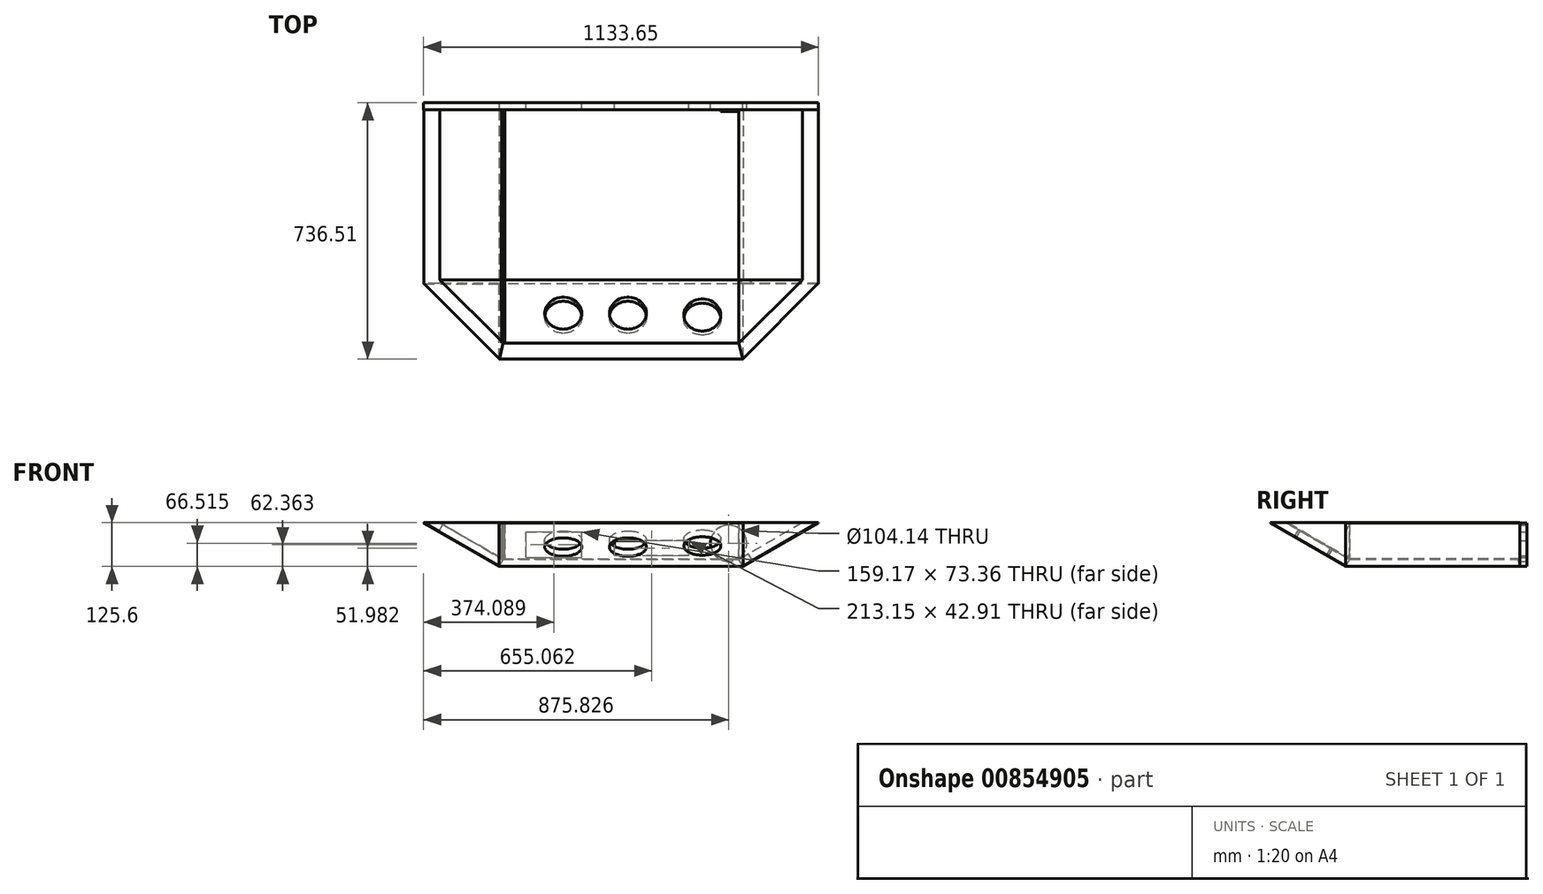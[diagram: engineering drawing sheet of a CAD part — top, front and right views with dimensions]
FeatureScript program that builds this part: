
annotation { "Feature Type Name" : "Feature", "Feature Type Description" : "" }
export const myFeature = defineFeature(function(context is Context, id is Id, definition is map)
    precondition{}
    {
        {
            var Q0;
            Q0=qCreatedBy(makeId("Top.planeOp"),FACE);
            var sketch = newSketch(context, id + "F0", { "sketchPlane" : qUnion([Q0])});
            skLineSegment(sketch, "E0.bottom", {"start": v(350, 250) * mm, "end": v(-350, 250) * mm});
            skLineSegment(sketch, "E0.top", {"start": v(350, -250) * mm, "end": v(-350, -250) * mm});
            skLineSegment(sketch, "E0.left", {"start": v(350, 250) * mm, "end": v(350, -250) * mm});
            skLineSegment(sketch, "E0.right", {"start": v(-350, 250) * mm, "end": v(-350, -250) * mm});
            skPoint(sketch, "E0.middle", {"position": v(0, 0) * mm});
            skSolve(sketch);
        }
        {
            var Q0;
            Q0=makeQuery(id+"F0.imprint","IMPRINT",FACE,{"disambiguationData":[TD([[makeQuery(id+"F0.imprint","IMPRINT",EDGE,{"derivedFrom":sQuery(id+"F0.wireOp",EDGE,"E0.bottom")}),1.0]])]});
            extrude(context, id + "F1", {"entities" : qUnion([Q0]), "depth" : 20 * mm, "offsetDistance" : 25 * mm});
        }
        {
            var Q0;
            Q0=makeQuery(id+"F1.opExtrude","CAP_EDGE",EDGE,{"disambiguationData":[OSD([sQuery(id+"F0.wireOp",EDGE,"E0.right")])],"isStart":false});
            var Q1;
            Q1=makeQuery(id+"F1.opExtrude","CAP_EDGE",EDGE,{"disambiguationData":[OSD([sQuery(id+"F0.wireOp",EDGE,"E0.top")])],"isStart":false});
            var Q2;
            Q2=makeQuery(id+"F1.opExtrude","CAP_EDGE",EDGE,{"disambiguationData":[OSD([sQuery(id+"F0.wireOp",EDGE,"E0.left")])],"isStart":false});
            chamfer(context, id + "F2", {"entities" : qUnion([Q0, Q1, Q2]), "chamferType" : ChamferType.OFFSET_ANGLE, "width" : 20 * mm, "oppositeDirection" : true, "angle" : 30 * degree, "tangentPropagation" : true});
        }
        {
            var Q0;
            Q0=makeQuery(id+"F2.opChamfer","BLEND_FACE",FACE,{"disambiguationData":[OSD([sQuery(id+"F0.wireOp",EDGE,"E0.top")])]});
            extrude(context, id + "F3", {"entities" : qUnion([Q0]), "operationType" : NewBodyOperationType.ADD, "depth" : 250 * mm, "offsetDistance" : 25 * mm});
        }
        {
            var Q0;
            Q0=makeQuery(id+"F2.opChamfer","BLEND_FACE",FACE,{"disambiguationData":[OSD([sQuery(id+"F0.wireOp",EDGE,"E0.right")])]});
            extrude(context, id + "F4", {"entities" : qUnion([Q0]), "operationType" : NewBodyOperationType.ADD, "depth" : 250 * mm, "offsetDistance" : 25 * mm});
        }
        {
            var Q0;
            Q0=makeQuery(id+"F2.opChamfer","BLEND_FACE",FACE,{"disambiguationData":[OSD([sQuery(id+"F0.wireOp",EDGE,"E0.left")])]});
            extrude(context, id + "F5", {"entities" : qUnion([Q0]), "operationType" : NewBodyOperationType.ADD, "depth" : 250 * mm, "offsetDistance" : 25 * mm});
        }
        {
            var Q0;
            {var subQ0=sQuery(id+"F0.wireOp",EDGE,"E0.right");var subQ1=sQuery(id+"F0.wireOp",EDGE,"E0.left");var subQ2=sQuery(id+"F0.wireOp",EDGE,"E0.top");var subQ3=sQuery(id+"F0.wireOp",EDGE,"E0.bottom");var subQ4=makeQuery(id+"F2.opChamfer","BLEND_VERTEX",VERTEX,{"blendedFrom":[makeQuery(id+"F1.opExtrude","CAP_EDGE",EDGE,{"disambiguationData":[OSD([subQ2])],"isStart":false}),makeQuery(id+"F1.opExtrude","CAP_EDGE",EDGE,{"disambiguationData":[OSD([subQ1])],"isStart":false}),makeQuery(id+"F1.opExtrude","CAP_FACE",FACE,{"disambiguationData":[OSD([subQ3,subQ2,subQ1,subQ0])],"isStart":false})],"blendedInto":[makeQuery(id+"F1.opExtrude","CAP_FACE",FACE,{"disambiguationData":[OSD([subQ3,subQ2,subQ1,subQ0])],"isStart":false})]});var subQ5=makeQuery(id+"F3.boolean.opBoolean","MERGE",VERTEX,{"derivedFrom":[subQ4,makeQuery(id+"F3.opExtrude","CAP_VERTEX",VERTEX,{"disambiguationData":[OSD([subQ3,subQ2,subQ1,subQ0]),TDD([subQ4])],"isStart":true})]});Q0=makeQuery(id+"F5.boolean.opBoolean","MERGE",VERTEX,{"derivedFrom":[subQ5,makeQuery(id+"F5.opExtrude","CAP_VERTEX",VERTEX,{"disambiguationData":[OSD([subQ3,subQ2,subQ1,subQ0]),TDD([subQ5])],"isStart":true})]});}
            var Q1;
            {var subQ0=sQuery(id+"F0.wireOp",EDGE,"E0.right");var subQ1=sQuery(id+"F0.wireOp",EDGE,"E0.left");var subQ2=sQuery(id+"F0.wireOp",EDGE,"E0.top");var subQ3=sQuery(id+"F0.wireOp",EDGE,"E0.bottom");Q1=makeQuery(id+"F3.opExtrude","CAP_VERTEX",VERTEX,{"disambiguationData":[OSD([subQ3,subQ2,subQ1,subQ0]),TDD([makeQuery(id+"F2.opChamfer","BLEND_VERTEX",VERTEX,{"blendedFrom":[makeQuery(id+"F1.opExtrude","CAP_EDGE",EDGE,{"disambiguationData":[OSD([subQ2])],"isStart":false}),makeQuery(id+"F1.opExtrude","CAP_EDGE",EDGE,{"disambiguationData":[OSD([subQ1])],"isStart":false}),makeQuery(id+"F1.opExtrude","CAP_FACE",FACE,{"disambiguationData":[OSD([subQ3,subQ2,subQ1,subQ0])],"isStart":false})],"blendedInto":[makeQuery(id+"F1.opExtrude","CAP_FACE",FACE,{"disambiguationData":[OSD([subQ3,subQ2,subQ1,subQ0])],"isStart":false})]})])],"isStart":false});}
            var Q2;
            {var subQ0=sQuery(id+"F0.wireOp",EDGE,"E0.right");var subQ1=sQuery(id+"F0.wireOp",EDGE,"E0.left");var subQ2=sQuery(id+"F0.wireOp",EDGE,"E0.top");var subQ3=sQuery(id+"F0.wireOp",EDGE,"E0.bottom");var subQ4=makeQuery(id+"F2.opChamfer","BLEND_VERTEX",VERTEX,{"blendedFrom":[makeQuery(id+"F1.opExtrude","CAP_EDGE",EDGE,{"disambiguationData":[OSD([subQ2])],"isStart":false}),makeQuery(id+"F1.opExtrude","CAP_EDGE",EDGE,{"disambiguationData":[OSD([subQ1])],"isStart":false}),makeQuery(id+"F1.opExtrude","CAP_FACE",FACE,{"disambiguationData":[OSD([subQ3,subQ2,subQ1,subQ0])],"isStart":false})],"blendedInto":[makeQuery(id+"F1.opExtrude","CAP_FACE",FACE,{"disambiguationData":[OSD([subQ3,subQ2,subQ1,subQ0])],"isStart":false})]});Q2=makeQuery(id+"F5.opExtrude","CAP_VERTEX",VERTEX,{"disambiguationData":[OSD([subQ3,subQ2,subQ1,subQ0]),TDD([makeQuery(id+"F3.boolean.opBoolean","MERGE",VERTEX,{"derivedFrom":[subQ4,makeQuery(id+"F3.opExtrude","CAP_VERTEX",VERTEX,{"disambiguationData":[OSD([subQ3,subQ2,subQ1,subQ0]),TDD([subQ4])],"isStart":true})]})])],"isStart":false});}
            cPlane(context, id + "F6", {"entities" : qUnion([Q0, Q1, Q2]), "cplaneType" : CPlaneType.THREE_POINT, "offset" : 0 * mm, "width" : 150 * mm, "height" : 150 * mm});
        }
        {
            var Q0;
            Q0=qCreatedBy(id+"F6.planeOp",FACE);
            var sketch = newSketch(context, id + "F7", { "sketchPlane" : qUnion([Q0])});
            skLineSegment(sketch, "E1", {"start": v(499.22, 278.94) * mm, "end": v(257.18, 216.53) * mm});
            skLineSegment(sketch, "E2", {"start": v(257.18, 216.53) * mm, "end": v(257.18, 466.29) * mm});
            skLineSegment(sketch, "E3", {"start": v(257.18, 466.29) * mm, "end": v(499.22, 278.94) * mm});
            skSolve(sketch);
        }
        {
            var Q0;
            Q0=makeQuery(id+"F7.imprint","IMPRINT",FACE,{"disambiguationData":[TD([[makeQuery(id+"F7.imprint","IMPRINT",EDGE,{"derivedFrom":sQuery(id+"F7.wireOp",EDGE,"E1")}),-1.0]])]});
            extrude(context, id + "F8", {"entities" : qUnion([Q0]), "operationType" : NewBodyOperationType.ADD, "depth" : 25 * mm, "offsetDistance" : 25 * mm});
        }
        {
            var Q0;
            {var subQ0=sQuery(id+"F0.wireOp",EDGE,"E0.right");var subQ1=sQuery(id+"F0.wireOp",EDGE,"E0.left");var subQ2=sQuery(id+"F0.wireOp",EDGE,"E0.top");var subQ3=sQuery(id+"F0.wireOp",EDGE,"E0.bottom");var subQ4=makeQuery(id+"F2.opChamfer","BLEND_VERTEX",VERTEX,{"blendedFrom":[makeQuery(id+"F1.opExtrude","CAP_EDGE",EDGE,{"disambiguationData":[OSD([subQ2])],"isStart":false}),makeQuery(id+"F1.opExtrude","CAP_EDGE",EDGE,{"disambiguationData":[OSD([subQ0])],"isStart":false}),makeQuery(id+"F1.opExtrude","CAP_FACE",FACE,{"disambiguationData":[OSD([subQ3,subQ2,subQ1,subQ0])],"isStart":false})],"blendedInto":[makeQuery(id+"F1.opExtrude","CAP_FACE",FACE,{"disambiguationData":[OSD([subQ3,subQ2,subQ1,subQ0])],"isStart":false})]});Q0=makeQuery(id+"F4.opExtrude","CAP_VERTEX",VERTEX,{"disambiguationData":[OSD([subQ3,subQ2,subQ1,subQ0]),TDD([makeQuery(id+"F3.boolean.opBoolean","MERGE",VERTEX,{"derivedFrom":[subQ4,makeQuery(id+"F3.opExtrude","CAP_VERTEX",VERTEX,{"disambiguationData":[OSD([subQ3,subQ2,subQ1,subQ0]),TDD([subQ4])],"isStart":true})]})])],"isStart":false});}
            var Q1;
            {var subQ0=sQuery(id+"F0.wireOp",EDGE,"E0.right");var subQ1=sQuery(id+"F0.wireOp",EDGE,"E0.left");var subQ2=sQuery(id+"F0.wireOp",EDGE,"E0.top");var subQ3=sQuery(id+"F0.wireOp",EDGE,"E0.bottom");var subQ4=makeQuery(id+"F2.opChamfer","BLEND_VERTEX",VERTEX,{"blendedFrom":[makeQuery(id+"F1.opExtrude","CAP_EDGE",EDGE,{"disambiguationData":[OSD([subQ2])],"isStart":false}),makeQuery(id+"F1.opExtrude","CAP_EDGE",EDGE,{"disambiguationData":[OSD([subQ0])],"isStart":false}),makeQuery(id+"F1.opExtrude","CAP_FACE",FACE,{"disambiguationData":[OSD([subQ3,subQ2,subQ1,subQ0])],"isStart":false})],"blendedInto":[makeQuery(id+"F1.opExtrude","CAP_FACE",FACE,{"disambiguationData":[OSD([subQ3,subQ2,subQ1,subQ0])],"isStart":false})]});var subQ5=makeQuery(id+"F3.boolean.opBoolean","MERGE",VERTEX,{"derivedFrom":[subQ4,makeQuery(id+"F3.opExtrude","CAP_VERTEX",VERTEX,{"disambiguationData":[OSD([subQ3,subQ2,subQ1,subQ0]),TDD([subQ4])],"isStart":true})]});Q1=makeQuery(id+"F4.boolean.opBoolean","MERGE",VERTEX,{"derivedFrom":[subQ5,makeQuery(id+"F4.opExtrude","CAP_VERTEX",VERTEX,{"disambiguationData":[OSD([subQ3,subQ2,subQ1,subQ0]),TDD([subQ5])],"isStart":true})]});}
            var Q2;
            {var subQ0=sQuery(id+"F0.wireOp",EDGE,"E0.right");var subQ1=sQuery(id+"F0.wireOp",EDGE,"E0.left");var subQ2=sQuery(id+"F0.wireOp",EDGE,"E0.top");var subQ3=sQuery(id+"F0.wireOp",EDGE,"E0.bottom");Q2=makeQuery(id+"F3.opExtrude","CAP_VERTEX",VERTEX,{"disambiguationData":[OSD([subQ3,subQ2,subQ1,subQ0]),TDD([makeQuery(id+"F2.opChamfer","BLEND_VERTEX",VERTEX,{"blendedFrom":[makeQuery(id+"F1.opExtrude","CAP_EDGE",EDGE,{"disambiguationData":[OSD([subQ2])],"isStart":false}),makeQuery(id+"F1.opExtrude","CAP_EDGE",EDGE,{"disambiguationData":[OSD([subQ0])],"isStart":false}),makeQuery(id+"F1.opExtrude","CAP_FACE",FACE,{"disambiguationData":[OSD([subQ3,subQ2,subQ1,subQ0])],"isStart":false})],"blendedInto":[makeQuery(id+"F1.opExtrude","CAP_FACE",FACE,{"disambiguationData":[OSD([subQ3,subQ2,subQ1,subQ0])],"isStart":false})]})])],"isStart":false});}
            cPlane(context, id + "F9", {"entities" : qUnion([Q0, Q1, Q2]), "cplaneType" : CPlaneType.THREE_POINT, "offset" : 25 * mm, "width" : 150 * mm, "height" : 150 * mm});
        }
        {
            var Q0;
            Q0=qCreatedBy(id+"F9.planeOp",FACE);
            var sketch = newSketch(context, id + "F10", { "sketchPlane" : qUnion([Q0])});
            skLineSegment(sketch, "E4", {"start": v(-257.22, -466.76) * mm, "end": v(-257.22, -216.6) * mm});
            skLineSegment(sketch, "E5", {"start": v(-257.22, -216.6) * mm, "end": v(-499.42, -279.04) * mm});
            skLineSegment(sketch, "E6", {"start": v(-499.42, -279.04) * mm, "end": v(-257.22, -466.76) * mm});
            skSolve(sketch);
        }
        {
            var Q0;
            Q0=makeQuery(id+"F10.imprint","IMPRINT",FACE,{"disambiguationData":[TD([[makeQuery(id+"F10.imprint","IMPRINT",EDGE,{"derivedFrom":sQuery(id+"F10.wireOp",EDGE,"E4")}),1.0]])]});
            extrude(context, id + "F11", {"entities" : qUnion([Q0]), "operationType" : NewBodyOperationType.ADD, "oppositeDirection" : true, "depth" : 25 * mm, "offsetDistance" : 25 * mm});
        }
        {
            var Q0;
            {var subQ0=sQuery(id+"F0.wireOp",EDGE,"E0.bottom");Q0=makeQuery(id+"F5.boolean.opBoolean","MERGE",FACE,{"derivedFrom":[makeQuery(id+"F4.boolean.opBoolean","MERGE",FACE,{"derivedFrom":[makeQuery(id+"F1.opExtrude","SWEPT_FACE",FACE,{"disambiguationData":[OSD([subQ0])]}),makeQuery(id+"F4.opExtrude","SWEPT_FACE",FACE,{"disambiguationData":[OSD([subQ0,sQuery(id+"F0.wireOp",EDGE,"E0.right")])]})]}),makeQuery(id+"F5.opExtrude","SWEPT_FACE",FACE,{"disambiguationData":[OSD([subQ0,sQuery(id+"F0.wireOp",EDGE,"E0.left")])]})]});}
            var Q1;
            Q1 = qBodyType(qCreatedBy(id + "F13" ,EDGE), BodyType.WIRE);
            cPlane(context, id + "F12", {"entities" : qUnion([Q0, Q1]), "cplaneType" : CPlaneType.OFFSET, "offset" : 0 * mm, "width" : 150 * mm, "height" : 150 * mm});
        }
        {
            var Q0;
            Q0=qCreatedBy(id+"F12.planeOp",FACE);
            var sketch = newSketch(context, id + "F13", { "sketchPlane" : qUnion([Q0])});
            skLineSegment(sketch, "E7", {"start": v(-566.59, 125.24) * mm, "end": v(567.06, 125.24) * mm});
            skLineSegment(sketch, "E8", {"start": v(567.06, 125.24) * mm, "end": v(349.95, 0) * mm});
            skLineSegment(sketch, "E9", {"start": v(349.95, 0) * mm, "end": v(-347.9, 0) * mm});
            skLineSegment(sketch, "E10", {"start": v(-347.9, 0) * mm, "end": v(-566.59, 125.24) * mm});
            skSolve(sketch);
        }
        {
            var Q0;
            Q0=makeQuery(id+"F13.imprint","IMPRINT",FACE,{"disambiguationData":[TD([[makeQuery(id+"F13.imprint","IMPRINT",EDGE,{"derivedFrom":sQuery(id+"F13.wireOp",EDGE,"E7")}),-1.0]])]});
            extrude(context, id + "F14", {"entities" : qUnion([Q0]), "depth" : 20 * mm, "offsetDistance" : 25 * mm});
        }
        {
            var Q0;
            Q0=qCreatedBy(id+"F12.planeOp",FACE);
            var sketch = newSketch(context, id + "F15", { "sketchPlane" : qUnion([Q0])});
            skLineSegment(sketch, "E11.bottom", {"start": v(-566.55, 125.42) * mm, "end": v(567.42, 125.42) * mm});
            skLineSegment(sketch, "E11.top", {"start": v(-566.55, 149.99) * mm, "end": v(567.42, 149.99) * mm});
            skLineSegment(sketch, "E11.left", {"start": v(-566.55, 125.42) * mm, "end": v(-566.55, 149.99) * mm});
            skLineSegment(sketch, "E11.right", {"start": v(567.42, 125.42) * mm, "end": v(567.42, 149.99) * mm});
            skSolve(sketch);
        }
        {
            var Q0;
            Q0=makeQuery(id+"F15.imprint","IMPRINT",FACE,{"disambiguationData":[TD([[makeQuery(id+"F15.imprint","IMPRINT",EDGE,{"derivedFrom":sQuery(id+"F15.wireOp",EDGE,"E11.bottom")}),1.0]])]});
            extrude(context, id + "F16", {"entities" : qUnion([Q0]), "operationType" : NewBodyOperationType.REMOVE, "oppositeDirection" : true, "depth" : 800 * mm, "offsetDistance" : 25 * mm});
        }
        {
            var Q0;
            Q0=makeQuery(id+"F14.opExtrude","CAP_FACE",FACE,{"disambiguationData":[OSD([sQuery(id+"F13.wireOp",EDGE,"E7"),sQuery(id+"F13.wireOp",EDGE,"E8"),sQuery(id+"F13.wireOp",EDGE,"E9"),sQuery(id+"F13.wireOp",EDGE,"E10")])],"isStart":false});
            var sketch = newSketch(context, id + "F17", { "sketchPlane" : qUnion([Q0])});
            skLineSegment(sketch, "E12.bottom", {"start": v(272.56, 25.68) * mm, "end": v(113.39, 25.68) * mm});
            skLineSegment(sketch, "E12.top", {"start": v(272.56, 99.04) * mm, "end": v(113.39, 99.04) * mm});
            skLineSegment(sketch, "E12.left", {"start": v(272.56, 25.68) * mm, "end": v(272.56, 99.04) * mm});
            skLineSegment(sketch, "E12.right", {"start": v(113.39, 25.68) * mm, "end": v(113.39, 99.04) * mm});
            skPoint(sketch, "E12.middle", {"position": v(192.97, 62.36) * mm});
            skCircle(sketch, "E13", {"center": v(-308.77, 66.52) * mm, "radius": 52.07 * mm});
            skLineSegment(sketch, "E14.bottom", {"start": v(-194.58, 30.53) * mm, "end": v(18.57, 30.53) * mm});
            skLineSegment(sketch, "E14.top", {"start": v(-194.58, 73.44) * mm, "end": v(18.57, 73.44) * mm});
            skLineSegment(sketch, "E14.left", {"start": v(-194.58, 30.53) * mm, "end": v(-194.58, 73.44) * mm});
            skLineSegment(sketch, "E14.right", {"start": v(18.57, 30.53) * mm, "end": v(18.57, 73.44) * mm});
            skSolve(sketch);
        }
        {
            var Q0;
            Q0=makeQuery(id+"F17.imprint","IMPRINT",FACE,{"disambiguationData":[TD([[makeQuery(id+"F17.imprint","IMPRINT",EDGE,{"derivedFrom":sQuery(id+"F17.wireOp",EDGE,"E13")}),1.0]])]});
            var Q1;
            Q1=makeQuery(id+"F17.imprint","IMPRINT",FACE,{"disambiguationData":[TD([[makeQuery(id+"F17.imprint","IMPRINT",EDGE,{"derivedFrom":sQuery(id+"F17.wireOp",EDGE,"E14.bottom")}),1.0]])]});
            var Q2;
            Q2=makeQuery(id+"F17.imprint","IMPRINT",FACE,{"disambiguationData":[TD([[makeQuery(id+"F17.imprint","IMPRINT",EDGE,{"derivedFrom":sQuery(id+"F17.wireOp",EDGE,"E12.bottom")}),-1.0]])]});
            extrude(context, id + "F18", {"entities" : qUnion([Q0, Q1, Q2]), "operationType" : NewBodyOperationType.REMOVE, "oppositeDirection" : true, "depth" : 25 * mm, "offsetDistance" : 25 * mm});
        }
        {
            var Q0;
            {var subQ0=sQuery(id+"F0.wireOp",EDGE,"E0.right");var subQ1=sQuery(id+"F0.wireOp",EDGE,"E0.left");var subQ2=sQuery(id+"F0.wireOp",EDGE,"E0.top");var subQ3=sQuery(id+"F0.wireOp",EDGE,"E0.bottom");Q0=makeQuery(id+"F3.opExtrude","SWEPT_FACE",FACE,{"disambiguationData":[OSD([subQ3,subQ2,subQ1,subQ0]),TDD([makeQuery(id+"F2.opChamfer","BLEND_EDGE",EDGE,{"blendedFrom":[makeQuery(id+"F1.opExtrude","CAP_EDGE",EDGE,{"disambiguationData":[OSD([subQ2])],"isStart":false}),makeQuery(id+"F1.opExtrude","CAP_FACE",FACE,{"disambiguationData":[OSD([subQ3,subQ2,subQ1,subQ0])],"isStart":false})],"blendedInto":[makeQuery(id+"F1.opExtrude","CAP_FACE",FACE,{"disambiguationData":[OSD([subQ3,subQ2,subQ1,subQ0])],"isStart":false})]})])]});}
            var sketch = newSketch(context, id + "F19", { "sketchPlane" : qUnion([Q0])});
            skCircle(sketch, "E15", {"center": v(233.3, -333.75) * mm, "radius": 53.05 * mm});
            skCircle(sketch, "E16", {"center": v(19.55, -327.63) * mm, "radius": 53.05 * mm});
            skCircle(sketch, "E17", {"center": v(-166.06, -327.63) * mm, "radius": 53.05 * mm});
            skSolve(sketch);
        }
        {
            var Q0;
            Q0=makeQuery(id+"F19.imprint","IMPRINT",FACE,{"disambiguationData":[TD([[makeQuery(id+"F19.imprint","IMPRINT",EDGE,{"derivedFrom":sQuery(id+"F19.wireOp",EDGE,"E17")}),1.0]])]});
            var Q1;
            Q1=makeQuery(id+"F19.imprint","IMPRINT",FACE,{"disambiguationData":[TD([[makeQuery(id+"F19.imprint","IMPRINT",EDGE,{"derivedFrom":sQuery(id+"F19.wireOp",EDGE,"E16")}),1.0]])]});
            var Q2;
            Q2=makeQuery(id+"F19.imprint","IMPRINT",FACE,{"disambiguationData":[TD([[makeQuery(id+"F19.imprint","IMPRINT",EDGE,{"derivedFrom":sQuery(id+"F19.wireOp",EDGE,"E15")}),1.0]])]});
            extrude(context, id + "F20", {"entities" : qUnion([Q0, Q1, Q2]), "operationType" : NewBodyOperationType.REMOVE, "oppositeDirection" : true, "depth" : 30 * mm, "offsetDistance" : 25 * mm});
        }
        {
            var Q0;
            {var subQ0=sQuery(id+"F0.wireOp",EDGE,"E0.right");var subQ1=sQuery(id+"F0.wireOp",EDGE,"E0.left");var subQ2=sQuery(id+"F0.wireOp",EDGE,"E0.top");var subQ3=sQuery(id+"F0.wireOp",EDGE,"E0.bottom");var subQ4=makeQuery(id+"F2.opChamfer","BLEND_VERTEX",VERTEX,{"blendedFrom":[makeQuery(id+"F1.opExtrude","CAP_EDGE",EDGE,{"disambiguationData":[OSD([subQ0])],"isStart":false}),makeQuery(id+"F1.opExtrude","SWEPT_FACE",FACE,{"disambiguationData":[OSD([subQ3])]}),makeQuery(id+"F1.opExtrude","CAP_FACE",FACE,{"disambiguationData":[OSD([subQ3,subQ2,subQ1,subQ0])],"isStart":false})],"blendedInto":[makeQuery(id+"F1.opExtrude","SWEPT_FACE",FACE,{"disambiguationData":[OSD([subQ3])]}),makeQuery(id+"F1.opExtrude","CAP_FACE",FACE,{"disambiguationData":[OSD([subQ3,subQ2,subQ1,subQ0])],"isStart":false})]});Q0=makeQuery(id+"F4.boolean.opBoolean","MERGE",VERTEX,{"derivedFrom":[subQ4,makeQuery(id+"F4.opExtrude","CAP_VERTEX",VERTEX,{"disambiguationData":[OSD([subQ3,subQ2,subQ1,subQ0]),TDD([subQ4])],"isStart":true})]});}
            var Q1;
            Q1=makeQuery(id+"F11.opExtrude","CAP_VERTEX",VERTEX,{"disambiguationData":[OSD([sQuery(id+"F10.wireOp",EDGE,"E4"),sQuery(id+"F10.wireOp",EDGE,"E5")])],"isStart":true});
            var Q2;
            {var subQ0=sQuery(id+"F0.wireOp",EDGE,"E0.right");var subQ1=sQuery(id+"F0.wireOp",EDGE,"E0.left");var subQ2=sQuery(id+"F0.wireOp",EDGE,"E0.top");var subQ3=sQuery(id+"F0.wireOp",EDGE,"E0.bottom");Q2=makeQuery(id+"F16.boolean.opBoolean","INTERSECT",VERTEX,{"derivedFrom":[makeQuery(id+"F3.opExtrude","SWEPT_FACE",FACE,{"disambiguationData":[OSD([subQ2,subQ0])]}),makeQuery(id+"F3.opExtrude","SWEPT_FACE",FACE,{"disambiguationData":[OSD([subQ3,subQ2,subQ1,subQ0]),TDD([makeQuery(id+"F2.opChamfer","BLEND_EDGE",EDGE,{"blendedFrom":[makeQuery(id+"F1.opExtrude","CAP_EDGE",EDGE,{"disambiguationData":[OSD([subQ2])],"isStart":false}),makeQuery(id+"F1.opExtrude","CAP_FACE",FACE,{"disambiguationData":[OSD([subQ3,subQ2,subQ1,subQ0])],"isStart":false})],"blendedInto":[makeQuery(id+"F1.opExtrude","CAP_FACE",FACE,{"disambiguationData":[OSD([subQ3,subQ2,subQ1,subQ0])],"isStart":false})]})])]}),makeQuery(id+"F16.opExtrude","SWEPT_FACE",FACE,{"disambiguationData":[OSD([sQuery(id+"F15.wireOp",EDGE,"E11.bottom")])]})]});}
            cPlane(context, id + "F21", {"entities" : qUnion([Q0, Q1, Q2]), "cplaneType" : CPlaneType.THREE_POINT, "offset" : 25 * mm, "width" : 150 * mm, "height" : 150 * mm});
        }
        {
            var Q0;
            Q0=qCreatedBy(id+"F21.planeOp",FACE);
            var sketch = newSketch(context, id + "F22", { "sketchPlane" : qUnion([Q0])});
            skLineSegment(sketch, "E18", {"start": v(-420.96, 125.33) * mm, "end": v(-238.43, 19.71) * mm});
            skLineSegment(sketch, "E19", {"start": v(-238.43, 19.71) * mm, "end": v(249.95, 19.71) * mm});
            skLineSegment(sketch, "E20", {"start": v(249.95, 19.71) * mm, "end": v(249.95, 125.1) * mm});
            skLineSegment(sketch, "E21", {"start": v(249.95, 125.1) * mm, "end": v(-420.96, 125.33) * mm});
            skSolve(sketch);
        }
        {
            var Q0;
            Q0=makeQuery(id+"F22.imprint","IMPRINT",FACE,{"disambiguationData":[TD([[makeQuery(id+"F22.imprint","IMPRINT",EDGE,{"derivedFrom":sQuery(id+"F22.wireOp",EDGE,"E18")}),1.0]])]});
            extrude(context, id + "F23", {"entities" : qUnion([Q0]), "operationType" : NewBodyOperationType.ADD, "endBound" : BoundingType.SYMMETRIC, "depth" : 10 * mm, "offsetDistance" : 25 * mm});
        }
    });
